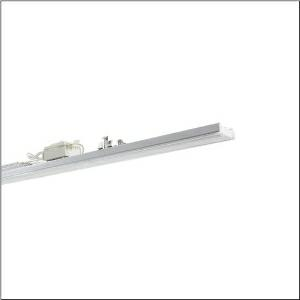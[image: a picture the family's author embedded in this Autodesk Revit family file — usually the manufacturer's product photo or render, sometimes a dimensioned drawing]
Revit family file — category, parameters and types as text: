
# Revit family: licross_r__21_recessed_ho_52te11cn4c5s_4dd9
name_source: partatom
category: Lighting Fixtures
units: mm (PartAtom-declared; Revit-internal decimal feet)

## family parameters
Cut with Voids When Loaded = No
Host = Face
Light Source = No
Part Type = Normal
Room Calculation Point = No
Round Connector Dimension = Use Diameter
Shared = No

## types (1)
- --- (1 x LED, 12640 lm, 68.4 W, 4000K)
    Apparent Load = 68 VA
    CIE Flux Codes = 87 95 99 100 100
    Color Rendering = 80
    Color Temperature = 4000K
    Default Elevation = 1800 mm
    Description = Licross® 21 Recessed HO, luminaire insert, of sheet steel, galvanised, coil coated, white, length: 1.500mm, width: 66mm, height: 67mm, LED rated luminous flux: 12.640lm, light colour: 840, control gear: ON/OFF Multilumen, CLOi, control gear: ECG Multilumen, with plug, 3-pole, with phase selection, mains connection: 220..240V, AC, 50/60Hz, start of lifetime: 68W, end of service life: 83W, internal wiring halogen-free, primary light control with lens, of plastic, primary optical cover: cover, of PMMA, light emission: direct distribution, primary light characteristic: symmetric, protection rating (complete): IP54, insulation class (complete): insulation class I (protective earthing), certification: CE, ENEC, VDE, UKCA, protection symbol: D if used in an environment with non-conductive dust loads with corresponding accessories, impact resistance: IK06, permissible ambient temperature for indoor applications: -35..+30°C, corresponds to IFS (International Featured Standards) requirements for safety and quality in the food industry, reducing of maximum allowable ambient temperature of 5°C with ceiling mounting, LABS conformity tested according to VDMA 24364:2018-05, packaging unit: 1 piece
    Height = 58 mm
    Lamp = 1 x LED
    Lamp Light Flux = 12640 lm
    Lamp Power = 68.4 W
    Lamp count = 1
    Length = 1500 mm
    Luminous efficacy = 185 lm/W
    Manufacturer = Siteco
    ModVariant = No
    Model = 52TE11CN4C5S
    Mounting Place = Ceiling
    Mounting Type = Pendant
    Number of Poles = 1
    OnlyDefault = Yes
    Power Factor = 1
    Product Name = Licross® 21 Recessed HO
    Product group = luminaire insert | ceiling pendant
    ProductGroupID = 902
    Protection Class = Protection class I
    Protection Degree = IP 54
    RLX_Detail_Level = 1
    RLX_Emergency_Light_Flux = 0 lm
    RLX_Emergency_Type = 0
    RLX_Emergency_Type_DB = No
    RlxData = <blob elided: 22377 chars, md5=9db72137>
    Socket = socket
    Standby Power = 0 W
    System Light Flux = 12640 lm
    System Power = 68 W
    Type Comments = factory setting: luminous flux: 100 % | (A | C | E) | 161 mA
    Type Image = l_1296930.jpg
    URL = http://relux.com
    VarID = @adj_132179
    Voltage = 0 V
    Weight = 0.00 kg
    Width = 66 mm

## geometry (parser evidence)
native form markers: Blend x4, Sweep x11
no freeform markers — native parametric forms only
